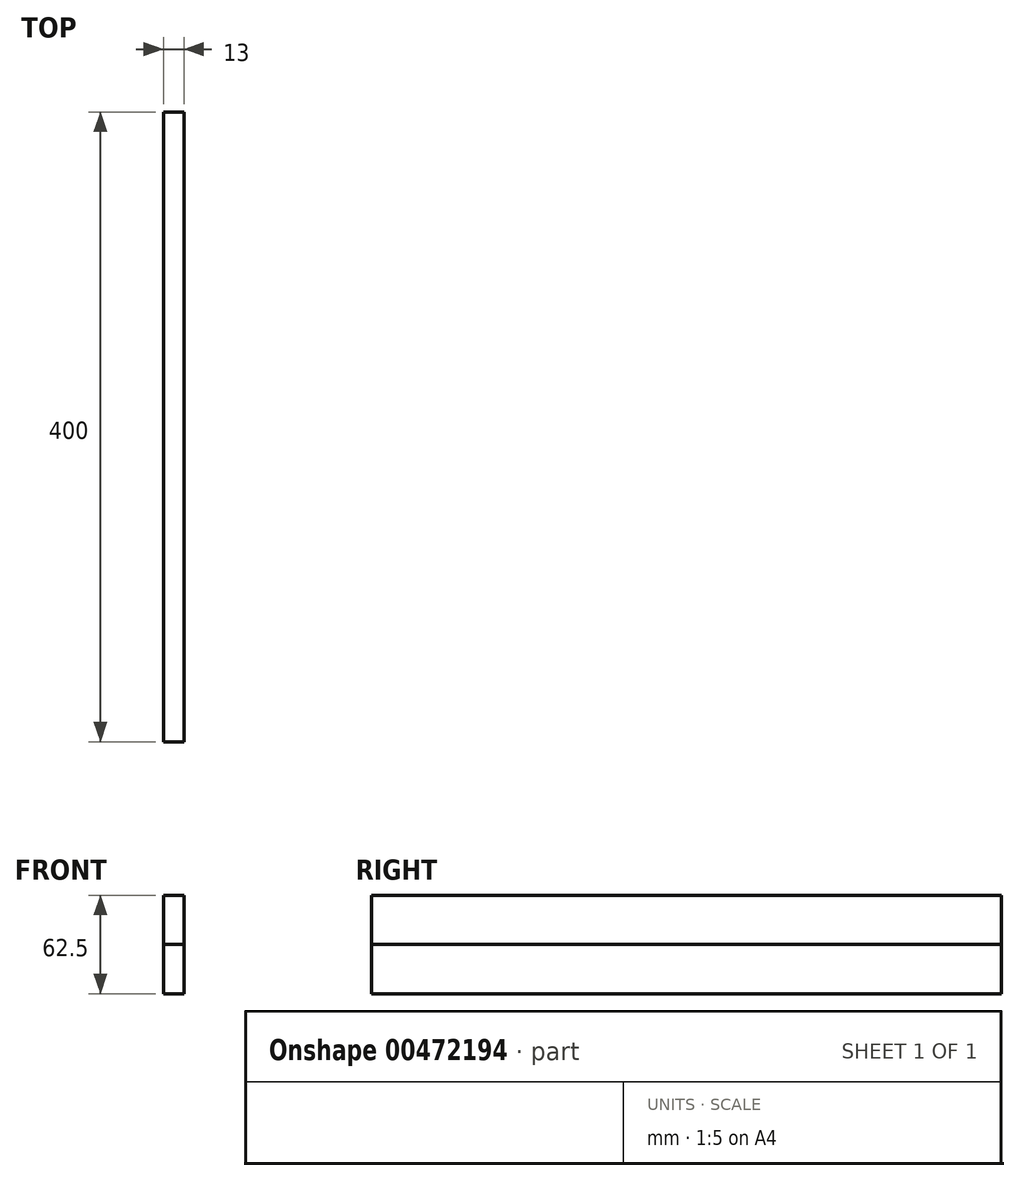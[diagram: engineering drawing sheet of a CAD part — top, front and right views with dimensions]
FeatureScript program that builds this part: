
annotation { "Feature Type Name" : "Feature", "Feature Type Description" : "" }
export const myFeature = defineFeature(function(context is Context, id is Id, definition is map)
    precondition{}
    {
        {
            var Q0;
            Q0=qCreatedBy(makeId("Front.planeOp"),FACE);
            var sketch = newSketch(context, id + "F0", { "sketchPlane" : qUnion([Q0])});
            skLineSegment(sketch, "E0.bottom", {"start": v(0, 0) * mm, "end": v(13, 0) * mm});
            skLineSegment(sketch, "E0.top", {"start": v(0, 31.25) * mm, "end": v(13, 31.25) * mm});
            skLineSegment(sketch, "E0.left", {"start": v(0, 0) * mm, "end": v(0, 31.25) * mm});
            skLineSegment(sketch, "E0.right", {"start": v(13, 0) * mm, "end": v(13, 31.25) * mm});
            skLineSegment(sketch, "E1.top", {"start": v(0, 62.5) * mm, "end": v(13, 62.5) * mm});
            skLineSegment(sketch, "E1.left", {"start": v(0, 31.25) * mm, "end": v(0, 62.5) * mm});
            skLineSegment(sketch, "E1.right", {"start": v(13, 31.25) * mm, "end": v(13, 62.5) * mm});
            skSolve(sketch);
        }
        {
            var Q0;
            Q0=makeQuery(id+"F0.imprint","IMPRINT",FACE,{"disambiguationData":[TD([[makeQuery(id+"F0.imprint","IMPRINT",EDGE,{"derivedFrom":sQuery(id+"F0.wireOp",EDGE,"E0.top")}),1.0]])]});
            extrude(context, id + "F1", {"entities" : qUnion([Q0]), "depth" : 400 * mm});
        }
        {
            var Q0;
            Q0=makeQuery(id+"F0.imprint","IMPRINT",FACE,{"disambiguationData":[TD([[makeQuery(id+"F0.imprint","IMPRINT",EDGE,{"derivedFrom":sQuery(id+"F0.wireOp",EDGE,"E0.bottom")}),1.0]])]});
            extrude(context, id + "F2", {"entities" : qUnion([Q0]), "depth" : 400 * mm});
        }
    });
